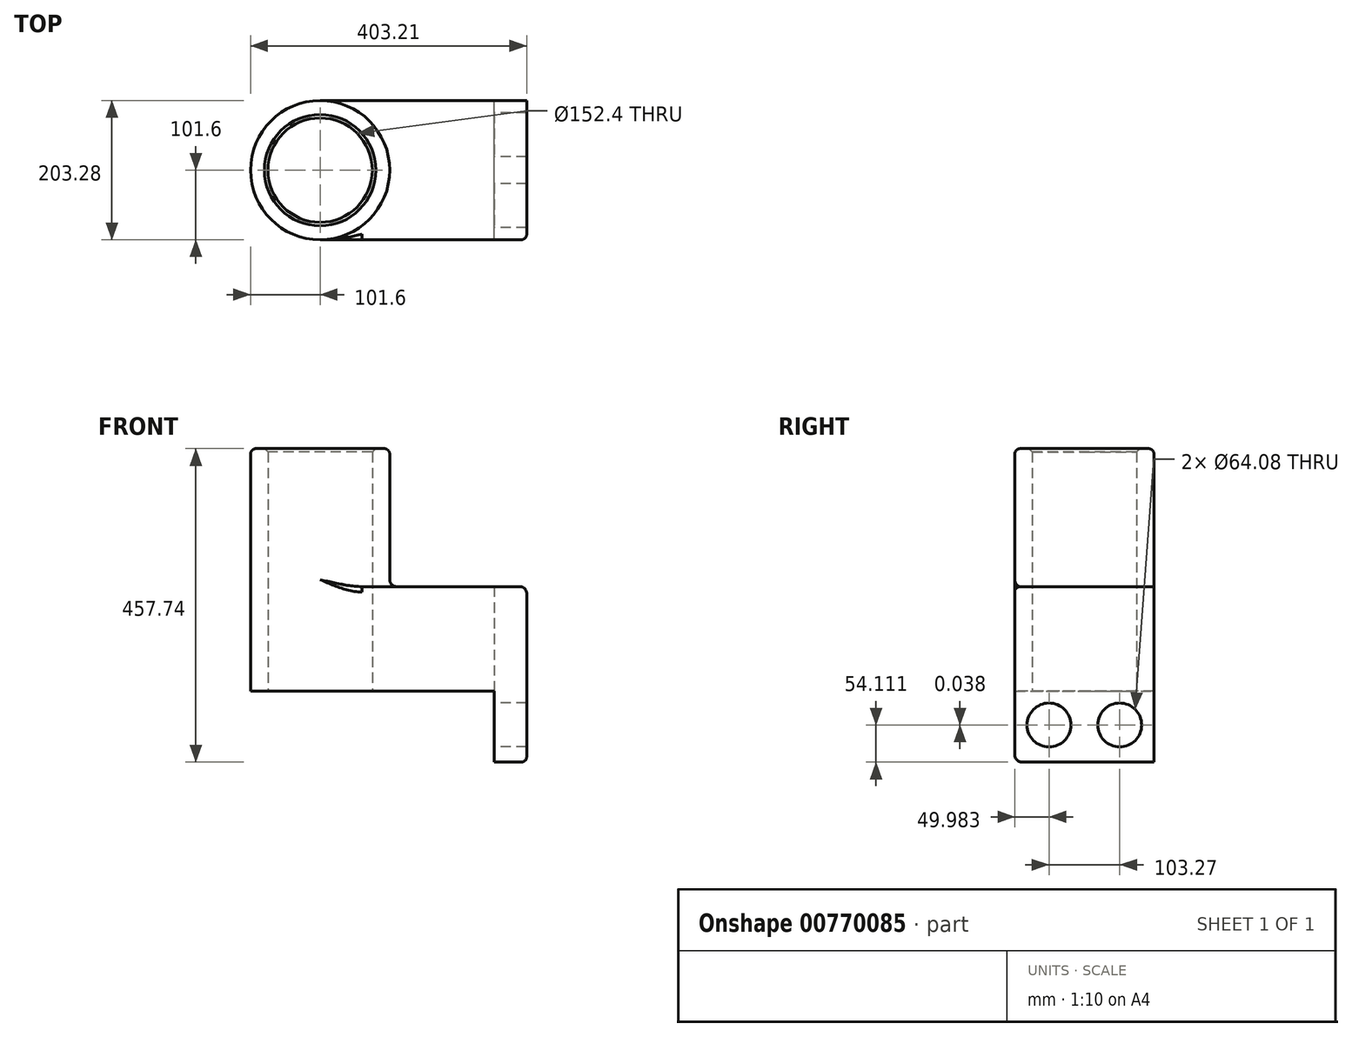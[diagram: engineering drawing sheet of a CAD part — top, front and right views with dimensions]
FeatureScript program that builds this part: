
annotation { "Feature Type Name" : "Feature", "Feature Type Description" : "" }
export const myFeature = defineFeature(function(context is Context, id is Id, definition is map)
    precondition{}
    {
        {
            var Q0;
            Q0=qCreatedBy(makeId("Top.planeOp"),FACE);
            var sketch = newSketch(context, id + "F0", { "sketchPlane" : qUnion([Q0])});
            skLineSegment(sketch, "E0.bottom", {"start": v(127, -101.6) * mm, "end": v(-127, -101.6) * mm});
            skLineSegment(sketch, "E0.top", {"start": v(127, 101.6) * mm, "end": v(-127, 101.6) * mm});
            skLineSegment(sketch, "E0.left", {"start": v(127, -101.6) * mm, "end": v(127, 101.6) * mm});
            skLineSegment(sketch, "E0.right", {"start": v(-127, -101.6) * mm, "end": v(-127, 101.6) * mm});
            skPoint(sketch, "E0.middle", {"position": v(0, 0) * mm});
            skPoint(sketch, "E1", {"position": v(-127, 0) * mm});
            skCircle(sketch, "E2", {"center": v(-127, 0) * mm, "radius": 101.6 * mm});
            skCircle(sketch, "E3", {"center": v(-127, 0) * mm, "radius": 76.2 * mm});
            skSolve(sketch);
        }
        {
            var Q0;
            {var subQ0=sQuery(id+"F0.wireOp",EDGE,"E0.bottom");Q0=makeQuery(id+"F0.imprint","IMPRINT",FACE,{"disambiguationData":[TD([[makeQuery(id+"F0.imprint","IMPRINT",EDGE,{"derivedFrom":subQ0}),-1.0]])]});}
            var Q1;
            {var subQ1=sQuery(id+"F0.wireOp",EDGE,"E0.right");var subQ3=sQuery(id+"F0.wireOp",EDGE,"E3");var subQ4=makeQuery(id+"F0.imprint","INTERSECT",VERTEX,{"disambiguationData":[OD(0.0)],"derivedFrom":[subQ1,subQ3]});Q1=makeQuery(id+"F0.imprint","IMPRINT",FACE,{"disambiguationData":[TD([[makeQuery(id+"F0.imprint","IMPRINT",EDGE,{"disambiguationData":[TD([[subQ4,-1.0]])],"derivedFrom":subQ3}),-1.0]])]});}
            var Q2;
            {var subQ1=sQuery(id+"F0.wireOp",EDGE,"E0.right");var subQ3=sQuery(id+"F0.wireOp",EDGE,"E3");var subQ4=makeQuery(id+"F0.imprint","INTERSECT",VERTEX,{"disambiguationData":[OD(0.0)],"derivedFrom":[subQ1,subQ3]});Q2=makeQuery(id+"F0.imprint","IMPRINT",FACE,{"disambiguationData":[TD([[makeQuery(id+"F0.imprint","IMPRINT",EDGE,{"disambiguationData":[TD([[subQ4,1.0]])],"derivedFrom":subQ3}),-1.0]])]});}
            extrude(context, id + "F1", {"entities" : qUnion([Q0, Q1, Q2]), "depth" : 152.4 * mm, "offsetDistance" : 25.4 * mm});
        }
        {
            var Q0;
            {var subQ1=sQuery(id+"F0.wireOp",EDGE,"E0.right");var subQ3=sQuery(id+"F0.wireOp",EDGE,"E3");var subQ4=makeQuery(id+"F0.imprint","INTERSECT",VERTEX,{"disambiguationData":[OD(0.0)],"derivedFrom":[subQ1,subQ3]});Q0=makeQuery(id+"F0.imprint","IMPRINT",FACE,{"disambiguationData":[TD([[makeQuery(id+"F0.imprint","IMPRINT",EDGE,{"disambiguationData":[TD([[subQ4,-1.0]])],"derivedFrom":subQ3}),-1.0]])]});}
            var Q1;
            {var subQ1=sQuery(id+"F0.wireOp",EDGE,"E0.right");var subQ3=sQuery(id+"F0.wireOp",EDGE,"E3");var subQ4=makeQuery(id+"F0.imprint","INTERSECT",VERTEX,{"disambiguationData":[OD(0.0)],"derivedFrom":[subQ1,subQ3]});Q1=makeQuery(id+"F0.imprint","IMPRINT",FACE,{"disambiguationData":[TD([[makeQuery(id+"F0.imprint","IMPRINT",EDGE,{"disambiguationData":[TD([[subQ4,1.0]])],"derivedFrom":subQ3}),-1.0]])]});}
            extrude(context, id + "F2", {"entities" : qUnion([Q0, Q1]), "operationType" : NewBodyOperationType.ADD, "depth" : 353.93 * mm, "offsetDistance" : 25.4 * mm});
        }
        {
            var Q0;
            Q0=makeQuery(id+"F1.opExtrude","SWEPT_FACE",FACE,{"disambiguationData":[OSD([sQuery(id+"F0.wireOp",EDGE,"E0.left")])]});
            var sketch = newSketch(context, id + "F3", { "sketchPlane" : qUnion([Q0])});
            skLineSegment(sketch, "E4.bottom", {"start": v(-101.6, 152.4) * mm, "end": v(101.68, 152.4) * mm});
            skLineSegment(sketch, "E4.top", {"start": v(-101.6, -103.81) * mm, "end": v(101.68, -103.81) * mm});
            skLineSegment(sketch, "E4.left", {"start": v(-101.6, 152.4) * mm, "end": v(-101.6, -103.81) * mm});
            skLineSegment(sketch, "E4.right", {"start": v(101.68, 152.4) * mm, "end": v(101.68, -103.81) * mm});
            skLineSegment(sketch, "E5.bottom", {"start": v(101.68, -103.81) * mm, "end": v(101.6, -103.81) * mm});
            skLineSegment(sketch, "E5.top", {"start": v(101.68, 0) * mm, "end": v(101.6, 0) * mm});
            skLineSegment(sketch, "E5.left", {"start": v(101.68, -103.81) * mm, "end": v(101.68, 0) * mm});
            skLineSegment(sketch, "E5.right", {"start": v(101.6, -103.81) * mm, "end": v(101.6, 0) * mm});
            skLineSegment(sketch, "E6.bottom", {"start": v(101.68, 24.3) * mm, "end": v(101.68, 24.3) * mm});
            skLineSegment(sketch, "E6.top", {"start": v(101.68, 55.72) * mm, "end": v(101.68, 55.72) * mm});
            skLineSegment(sketch, "E6.left", {"start": v(101.68, 24.3) * mm, "end": v(101.68, 55.72) * mm});
            skLineSegment(sketch, "E6.right", {"start": v(101.68, 24.3) * mm, "end": v(101.68, 55.72) * mm});
            skLineSegment(sketch, "E7", {"start": v(0, 0) * mm, "end": v(0.04, -103.81) * mm});
            skCircle(sketch, "E8", {"center": v(-51.62, -49.7) * mm, "radius": 32.04 * mm});
            skCircle(sketch, "E9.MirrorC", {"center": v(51.65, -49.66) * mm, "radius": 32.04 * mm});
            skSolve(sketch);
        }
        {
            var Q0;
            Q0 = qSketchRegion(id + "F3", true);
            extrude(context, id + "F4", {"entities" : qUnion([Q0]), "operationType" : NewBodyOperationType.ADD, "depth" : 47.6 * mm, "offsetDistance" : 25.4 * mm});
        }
        {
            var Q0;
            {var subQ0=sQuery(id+"F0.wireOp",EDGE,"E2");Q0=makeQuery(id+"F2.boolean.opBoolean","INTERSECT",EDGE,{"derivedFrom":[makeQuery(id+"F1.opExtrude","CAP_FACE",FACE,{"disambiguationData":[OSD([sQuery(id+"F0.wireOp",EDGE,"E0.bottom"),sQuery(id+"F0.wireOp",EDGE,"E0.top"),sQuery(id+"F0.wireOp",EDGE,"E0.left"),subQ0,sQuery(id+"F0.wireOp",EDGE,"E3")])],"isStart":false}),makeQuery(id+"F2.opExtrude","SWEPT_FACE",FACE,{"disambiguationData":[OSD([subQ0])]})]});}
            var Q1;
            Q1=makeQuery(id+"F4.opExtrude","SWEPT_EDGE",EDGE,{"disambiguationData":[OSD([sQuery(id+"F3.wireOp",EDGE,"E4.top"),sQuery(id+"F3.wireOp",EDGE,"E4.left")])]});
            var Q2;
            Q2=makeQuery(id+"F4.opExtrude","SWEPT_EDGE",EDGE,{"disambiguationData":[OSD([sQuery(id+"F3.wireOp",EDGE,"E5.bottom"),sQuery(id+"F3.wireOp",EDGE,"E5.left")])]});
            var Q3;
            Q3=makeQuery(id+"F4.opExtrude","CAP_EDGE",EDGE,{"disambiguationData":[OSD([sQuery(id+"F3.wireOp",EDGE,"E4.bottom")])],"isStart":false});
            fillet(context, id + "F5", {"entities" : qUnion([Q0, Q1, Q2, Q3]), "radius" : 10.16 * mm, "tangentPropagation" : true, "allowEdgeOverflow" : false});
        }
        {
            var Q0;
            Q0=makeQuery(id+"F2.opExtrude","CAP_EDGE",EDGE,{"disambiguationData":[OSD([sQuery(id+"F0.wireOp",EDGE,"E2")])],"isStart":false});
            var Q1;
            Q1=makeQuery(id+"F4.boolean.opBoolean","MERGE",EDGE,{"derivedFrom":[makeQuery(id+"F1.opExtrude","CAP_EDGE",EDGE,{"disambiguationData":[OSD([sQuery(id+"F0.wireOp",EDGE,"E0.bottom")])],"isStart":false}),makeQuery(id+"F4.opExtrude","SWEPT_EDGE",EDGE,{"disambiguationData":[OSD([sQuery(id+"F3.wireOp",EDGE,"E4.bottom"),sQuery(id+"F3.wireOp",EDGE,"E4.left")])]})]});
            fillet(context, id + "F6", {"entities" : qUnion([Q0, Q1]), "radius" : 7.93 * mm, "tangentPropagation" : true, "allowEdgeOverflow" : false});
        }
        {
            var Q0;
            Q0=makeQuery(id+"F2.opExtrude","CAP_EDGE",EDGE,{"disambiguationData":[OSD([sQuery(id+"F0.wireOp",EDGE,"E3")])],"isStart":false});
            chamfer(context, id + "F7", {"entities" : qUnion([Q0]), "width" : 5.08 * mm, "tangentPropagation" : true});
        }
    });
